# Revit family: BAS-IP_Вызывная панель_AV-06M
name_source: partatom
category: Устройства связи
units: mm (PartAtom-declared; Revit-internal decimal feet)

## family parameters
Всегда вертикально = Да
На основе рабочей плоскости = Нет
Общий = Нет
При загрузке вырезать с полостями = Нет
Размер круглого соединителя = Использовать диаметр
Сохранять ориентацию аннотаций = Нет
Тип детали = Нормальный
Точка расчета площади = Нет

## types (2) — shared parameters
ADSK_Единица измерения = шт.
ADSK_Завод-изготовитель = BAS-IP
ADSK_Количество = 1
ADSK_Наименование = Индивидуальная IP вызывная панель со считывателем Mifare
IK-код = IK06
Выходное видео = FullHD (1920 × 1080), H.264 Main Profile
Дисплей = Нет
Изготовитель = BAS-IP
Камера = 1/2.8”
Класс степени защиты = IP65
Корпус = Пластик
Минимальная освещенность = 0,01 Люкс
Ночная подсветка = 12 светодиодов
Питание = IEEE 803.2af PoE, +12 В постоянного тока
Потребление питания = 5,5 Вт, в режиме ожидания - 2,1 Вт
Размер под установку = 58 × 145 × 42 мм
Размер самой панели = 52 × 137 × 28 мм
Разрешение = 2 Мп
Температурный режим = -40 – +65 °С
Тип панели = Индивидуальная
Тип установки = Накладной монтаж с защитой от солнца и дождя или без (в комплекте)
Угол обзора камеры = 110° (по горизонтали)
Цветовое решение = Серебристый

## per-type parameters (varying)
| type | ADSK_Марка | ADSK_Материал |
| Серебристый | AV-06M Silver | Silver |
| Черный | AV-06M Black | Black silver |
